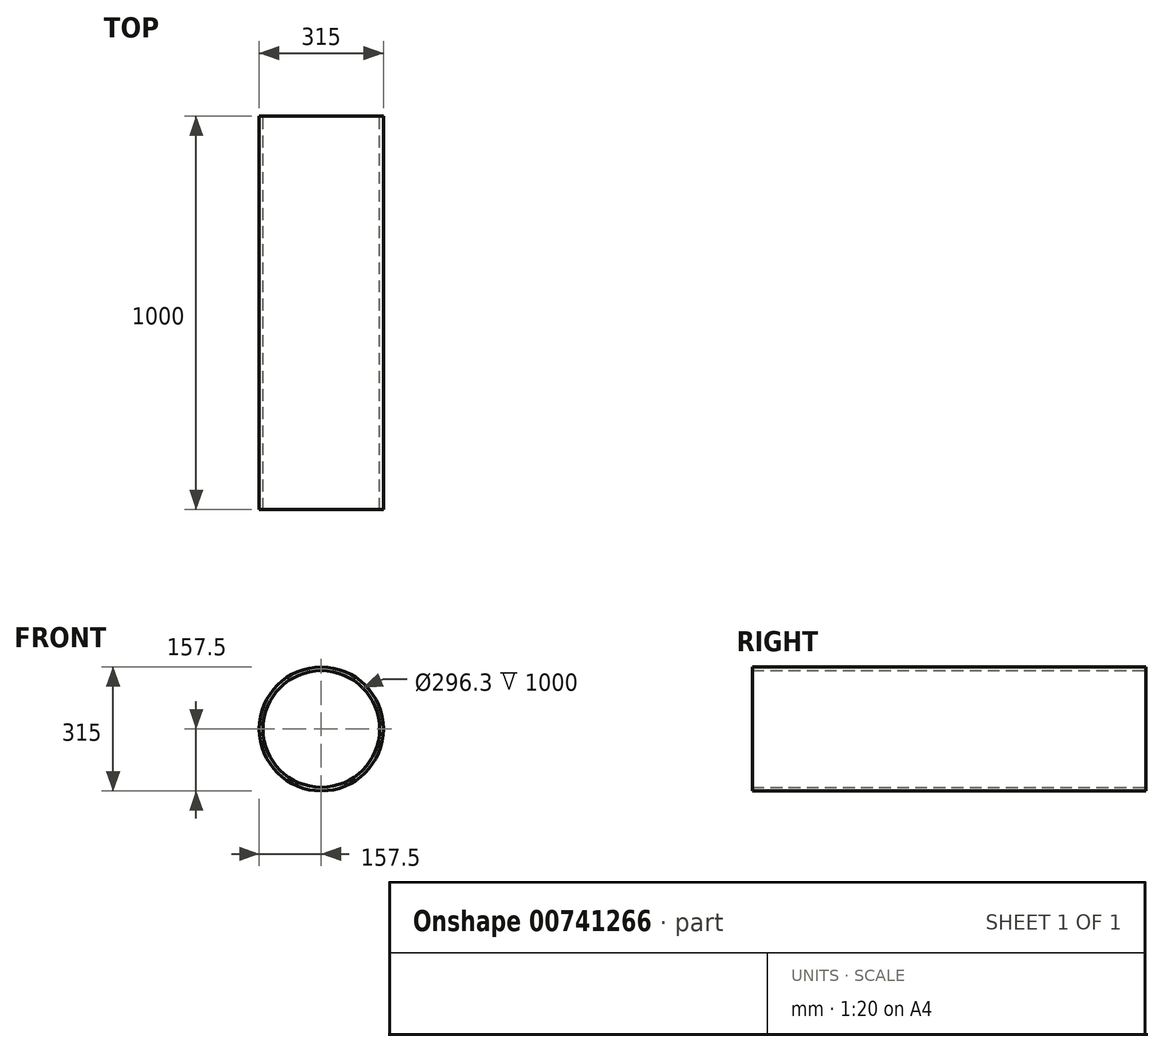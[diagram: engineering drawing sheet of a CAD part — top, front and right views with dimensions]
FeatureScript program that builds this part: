
annotation { "Feature Type Name" : "Feature", "Feature Type Description" : "" }
export const myFeature = defineFeature(function(context is Context, id is Id, definition is map)
    precondition{}
    {
        {
            var Q0;
            Q0=qCreatedBy(makeId("Front.planeOp"),FACE);
            var sketch = newSketch(context, id + "F0", { "sketchPlane" : qUnion([Q0])});
            skCircle(sketch, "E0", {"center": v(0, 0) * mm, "radius": 157.5 * mm});
            skCircle(sketch, "E1", {"center": v(0, 0) * mm, "radius": 148.15 * mm});
            skSolve(sketch);
        }
        {
            var Q0;
            Q0=makeQuery(id+"F0.imprint","IMPRINT",FACE,{"disambiguationData":[TD([[makeQuery(id+"F0.imprint","IMPRINT",EDGE,{"derivedFrom":sQuery(id+"F0.wireOp",EDGE,"E0")}),1.0]])]});
            extrude(context, id + "F1", {"entities" : qUnion([Q0]), "endBound" : BoundingType.SYMMETRIC, "depth" : 1000 * mm, "offsetDistance" : 25 * mm});
        }
    });
